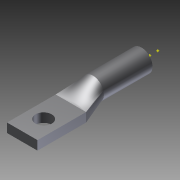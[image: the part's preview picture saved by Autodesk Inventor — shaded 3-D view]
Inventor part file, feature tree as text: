
AUTODESK INVENTOR PART (.ipt)
format: ipt  version: 2011 (Build 150239000, 239)  size: 134,144 bytes
history: native  units: mm
features: other x4, plane x2, imported_body x1, sketch x1
ambient origin geometry x8: Origin, YZ Plane, XZ Plane, XY Plane, X Axis, Y Axis, Z Axis, Center Point
bodies: Solid1 (feature_tree)
feature tree (8):
  imported_body  "Base1"
  sketch  "Sketch1"  dims[d0=3.175mm d1=6.35mm]
  other  "Work Point2"
  other  "Work Point3"
  plane  "Work Plane1"
  other  "Work Axis1"
  plane  "Work Plane2"
  other  "Work Axis2"
